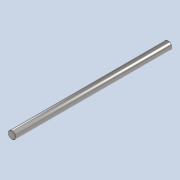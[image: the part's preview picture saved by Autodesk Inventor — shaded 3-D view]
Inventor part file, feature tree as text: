
AUTODESK INVENTOR PART (.ipt)
format: ipt  version: 2020 (Build 240168000, 168)  size: 80,384 bytes
history: native  units: mm
features: extrude x1, chamfer x1, sketch x1
ambient origin geometry x8: Origin, YZ Plane, XZ Plane, XY Plane, X Axis, Y Axis, Z Axis, Center Point
bodies: Solid1 (feature_tree)
feature tree (3):
  extrude  "Extrusion1"  Depth=163.0mm TaperAngle=0.0deg
  chamfer  "Chamfer1"  Distance=0.5mm Angle=45.0deg
  sketch  "Sketch1"  dims[d0=8.0mm d1=163.0mm d2=0.0mm d3=0.5mm d4=2.0mm d5=45.0deg]
